# Revit family: Shower-Valve_Trim-KALLISTA-One_Nazare-P23331
name_source: partatom
category: Specialty Equipment
units: mm (PartAtom-declared; Revit-internal decimal feet)

## family parameters
Cut with Voids When Loaded = No
Host = Face
OmniClass Number = 23.31.25.00
Part Type = Normal
Room Calculation Point = No
Round Connector Dimension = Use Diameter
Shared = No

## types (4) — shared parameters
ADA Compliant = Yes
Assembly Code = C1030200
Date Modified = 10/13/2024
Default Elevation = 42"
Description = Transfer Trim, Lever Handle
Handle Clearance = 2 7/8"
Height = 3 3/4"
Length = 3 3/8"
Manufacturer = Kallista Co.
Master Format 2014 = 10 28 00
Master Format 2014 Name = Toilet, Bath, and Laundry Accessories
Material = Brass Construction
Product Documentation Link = https://resources.kohler.com
Product Name = One Nazare
URL = https://www.kallista.com
WaterSense Certified = No
Width = 3 3/4"

## per-type parameters (varying)
| type | Finish | Model | Product Page URL | Type |
| BAF-Brushed French Gold | Kallista-Metal-BAF-Brushed_French_Gold | P23331-LV-BAF | https://www.kallista.com | 1 |
| CP-Chrome | Kallista-Metal-CP-Chrome | P23331-LV-CP | https://www.kallista.com | 2 |
| SN-Polished Nickel | Kallista-Metal-SN-Polished_Nickel | P23331-LV-SN | https://www.kallista.com | 3 |
| 2MB-Brushed Brass | Kallista-Metal-2MB- Brushed_Brass | P23331-LV-2MB |  | 4 |

## geometry (parser evidence)
native form markers: Sweep x5
no freeform markers — native parametric forms only
